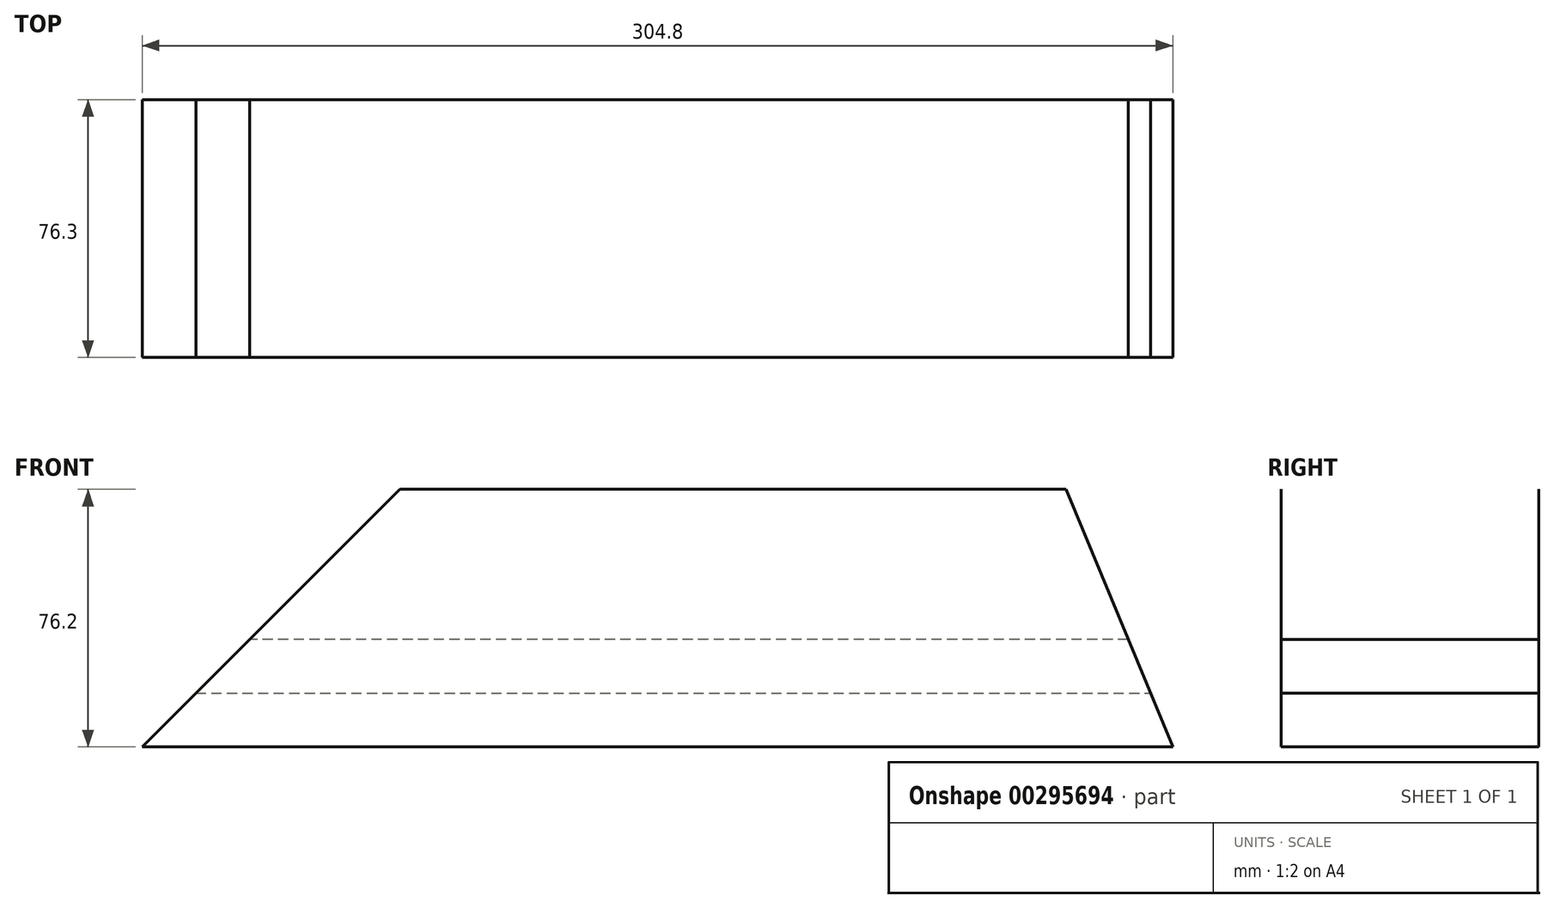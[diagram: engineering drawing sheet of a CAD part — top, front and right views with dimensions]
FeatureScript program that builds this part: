
annotation { "Feature Type Name" : "Feature", "Feature Type Description" : "" }
export const myFeature = defineFeature(function(context is Context, id is Id, definition is map)
    precondition{}
    {
        {
            var Q0;
            Q0=qCreatedBy(makeId("Front.planeOp"),FACE);
            cPlane(context, id + "F0", {"entities" : qUnion([Q0]), "cplaneType" : CPlaneType.OFFSET, "offset" : 38.1 * mm, "width" : 152.4 * mm, "height" : 152.4 * mm});
        }
        {
            var Q0;
            Q0=qCreatedBy(id+"F0.planeOp",FACE);
            var sketch = newSketch(context, id + "F1", { "sketchPlane" : qUnion([Q0])});
            skLineSegment(sketch, "E0.bottom", {"start": v(152.4, -38.1) * mm, "end": v(-152.4, -38.1) * mm});
            skLineSegment(sketch, "E0.top", {"start": v(152.4, 38.1) * mm, "end": v(-152.4, 38.1) * mm});
            skLineSegment(sketch, "E0.left", {"start": v(152.4, -38.1) * mm, "end": v(152.4, 38.1) * mm});
            skLineSegment(sketch, "E0.right", {"start": v(-152.4, -38.1) * mm, "end": v(-152.4, 38.1) * mm});
            skPoint(sketch, "E0.middle", {"position": v(0, 0) * mm});
            skSolve(sketch);
        }
        {
            var Q0;
            Q0 = qSketchRegion(id + "F1", true);
            extrude(context, id + "F2", {"entities" : qUnion([Q0]), "depth" : 5 / 203.2 * mm});
        }
        {
            var Q0;
            Q0=makeQuery(id+"F2.opExtrude","SWEPT_BODY",BODY,{"disambiguationData":[OSD([sQuery(id+"F1.wireOp",EDGE,"E0.bottom"),sQuery(id+"F1.wireOp",EDGE,"E0.top"),sQuery(id+"F1.wireOp",EDGE,"E0.left"),sQuery(id+"F1.wireOp",EDGE,"E0.right")])]});
            var Q1;
            Q1=makeQuery(id+"F2.opExtrude","CAP_FACE",FACE,{"disambiguationData":[OSD([sQuery(id+"F1.wireOp",EDGE,"E0.bottom"),sQuery(id+"F1.wireOp",EDGE,"E0.top"),sQuery(id+"F1.wireOp",EDGE,"E0.left"),sQuery(id+"F1.wireOp",EDGE,"E0.right")])],"isStart":false});
            mirror(context, id + "F3", {"entities" : qUnion([Q0]), "mirrorPlane" : qUnion([Q1])});
        }
        {
            var Q0;
            Q0=makeQuery(id+"F2.opExtrude","SWEPT_BODY",BODY,{"disambiguationData":[OSD([sQuery(id+"F1.wireOp",EDGE,"E0.bottom"),sQuery(id+"F1.wireOp",EDGE,"E0.top"),sQuery(id+"F1.wireOp",EDGE,"E0.left"),sQuery(id+"F1.wireOp",EDGE,"E0.right")])]});
            var Q1;
            Q1=makeQuery(id+"F3.opPattern","COPY",BODY,{"derivedFrom":makeQuery(id+"F2.opExtrude","SWEPT_BODY",BODY,{"disambiguationData":[OSD([sQuery(id+"F1.wireOp",EDGE,"E0.bottom"),sQuery(id+"F1.wireOp",EDGE,"E0.top"),sQuery(id+"F1.wireOp",EDGE,"E0.left"),sQuery(id+"F1.wireOp",EDGE,"E0.right")])]}),"instanceName":"1"});
            var Q2;
            Q2=qCreatedBy(makeId("Front.planeOp"),FACE);
            mirror(context, id + "F4", {"entities" : qUnion([Q0, Q1]), "mirrorPlane" : qUnion([Q2])});
        }
        {
            var Q0;
            Q0=qCreatedBy(id+"F0.planeOp",FACE);
            var sketch = newSketch(context, id + "F5", { "sketchPlane" : qUnion([Q0])});
            skLineSegment(sketch, "E1.0", {"start": v(152.4, -38.1) * mm, "end": v(-152.4, -38.1) * mm});
            skLineSegment(sketch, "E2", {"start": v(-152.4, -38.1) * mm, "end": v(-152.4, -38.1) * mm});
            skLineSegment(sketch, "E3", {"start": v(-152.4, -38.1) * mm, "end": v(152.4, -38.1) * mm});
            skLineSegment(sketch, "E4", {"start": v(152.4, -38.1) * mm, "end": v(152.4, -38.1) * mm});
            skLineSegment(sketch, "E5", {"start": v(-152.4, -38.1) * mm, "end": v(-152.4, -22.23) * mm});
            skLineSegment(sketch, "E6", {"start": v(-152.4, -22.23) * mm, "end": v(152.4, -22.23) * mm});
            skLineSegment(sketch, "E7", {"start": v(152.4, -22.23) * mm, "end": v(152.4, -38.1) * mm});
            skSolve(sketch);
        }
        {
            var Q0;
            Q0 = qSketchRegion(id + "F5", true);
            var Q1;
            Q1=makeQuery(id+"F4.opPattern","COPY",FACE,{"derivedFrom":makeQuery(id+"F2.opExtrude","CAP_FACE",FACE,{"disambiguationData":[OSD([sQuery(id+"F1.wireOp",EDGE,"E0.bottom"),sQuery(id+"F1.wireOp",EDGE,"E0.top"),sQuery(id+"F1.wireOp",EDGE,"E0.left"),sQuery(id+"F1.wireOp",EDGE,"E0.right")])],"isStart":true}),"instanceName":"1"});
            extrude(context, id + "F6", {"entities" : qUnion([Q0]), "endBound" : BoundingType.UP_TO_SURFACE, "oppositeDirection" : true, "endBoundEntityFace" : qUnion([Q1]), "depth" : 25.4 * mm});
        }
        {
            var Q0;
            Q0=makeQuery(id+"F6.opExtrude","SWEPT_BODY",BODY,{"disambiguationData":[OSD([sQuery(id+"F5.wireOp",EDGE,"E1.0"),sQuery(id+"F5.wireOp",EDGE,"E2"),sQuery(id+"F5.wireOp",EDGE,"E3"),sQuery(id+"F5.wireOp",EDGE,"E4")])]});
            var Q1;
            Q1=makeQuery(id+"F6.opExtrude","SWEPT_FACE",FACE,{"disambiguationData":[OSD([sQuery(id+"F5.wireOp",EDGE,"E6")])]});
            mirror(context, id + "F7", {"entities" : qUnion([Q0]), "mirrorPlane" : qUnion([Q1])});
        }
        {
            var Q0;
            Q0=qCreatedBy(makeId("Front.planeOp"),FACE);
            var sketch = newSketch(context, id + "F8", { "sketchPlane" : qUnion([Q0])});
            skLineSegment(sketch, "E8.0", {"start": v(-152.4, -38.1) * mm, "end": v(-152.4, 38.1) * mm});
            skLineSegment(sketch, "E9", {"start": v(-152.4, 38.1) * mm, "end": v(-76.2, 38.1) * mm});
            skLineSegment(sketch, "E10", {"start": v(-76.2, 38.1) * mm, "end": v(-152.4, -38.1) * mm});
            skLineSegment(sketch, "E11.0", {"start": v(152.4, -38.1) * mm, "end": v(152.4, 38.1) * mm});
            skLineSegment(sketch, "E12", {"start": v(152.4, 38.1) * mm, "end": v(120.84, 38.1) * mm});
            skLineSegment(sketch, "E13", {"start": v(120.84, 38.1) * mm, "end": v(152.4, -38.1) * mm});
            skSolve(sketch);
        }
        {
            var Q0;
            Q0 = qSketchRegion(id + "F8", true);
            extrude(context, id + "F9", {"entities" : qUnion([Q0]), "operationType" : NewBodyOperationType.REMOVE, "endBound" : BoundingType.THROUGH_ALL, "oppositeDirection" : true, "depth" : 25.4 * mm, "hasSecondDirection" : true, "secondDirectionBound" : SecondDirectionBoundingType.THROUGH_ALL, "secondDirectionOppositeDirection" : false, "secondDirectionDepth" : 25.4 * mm});
        }
    });
